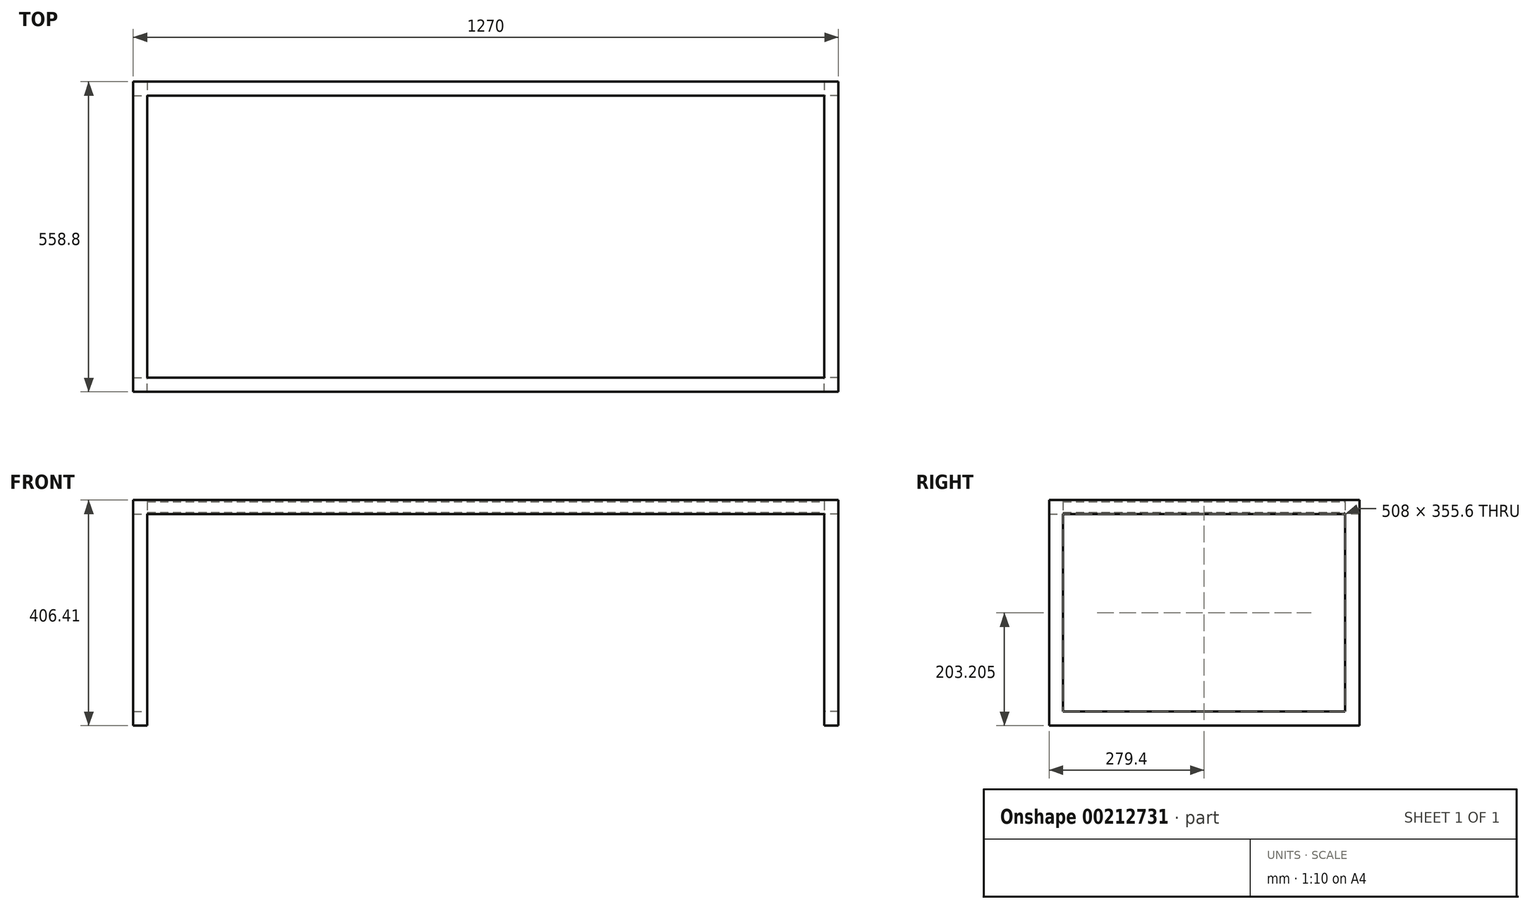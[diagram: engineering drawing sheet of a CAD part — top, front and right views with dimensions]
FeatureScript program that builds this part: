
annotation { "Feature Type Name" : "Feature", "Feature Type Description" : "" }
export const myFeature = defineFeature(function(context is Context, id is Id, definition is map)
    precondition{}
    {
        {
            var Q0;
            Q0=qCreatedBy(makeId("Top.planeOp"),FACE);
            var sketch = newSketch(context, id + "F0", { "sketchPlane" : qUnion([Q0])});
            skLineSegment(sketch, "E0.bottom", {"start": v(-609.6, -254) * mm, "end": v(609.6, -254) * mm});
            skLineSegment(sketch, "E0.top", {"start": v(-609.6, 254) * mm, "end": v(609.6, 254) * mm});
            skLineSegment(sketch, "E0.left", {"start": v(-609.6, -254) * mm, "end": v(-609.6, 254) * mm});
            skLineSegment(sketch, "E0.right", {"start": v(609.6, -254) * mm, "end": v(609.6, 254) * mm});
            skPoint(sketch, "E0.middle", {"position": v(0, 0) * mm});
            skSolve(sketch);
        }
        {
            var Q0;
            Q0=makeQuery(id+"F0.imprint","IMPRINT",FACE,{"disambiguationData":[TD([[makeQuery(id+"F0.imprint","IMPRINT",EDGE,{"derivedFrom":sQuery(id+"F0.wireOp",EDGE,"E0.bottom")}),1.0]])]});
            extrude(context, id + "F1", {"entities" : qUnion([Q0]), "depth" : 19.05 * mm});
        }
        {
            var Q0;
            Q0=makeQuery(id+"F1.opExtrude","CAP_FACE",FACE,{"disambiguationData":[OSD([sQuery(id+"F0.wireOp",EDGE,"E0.bottom"),sQuery(id+"F0.wireOp",EDGE,"E0.top"),sQuery(id+"F0.wireOp",EDGE,"E0.left"),sQuery(id+"F0.wireOp",EDGE,"E0.right")])],"isStart":true});
            cPlane(context, id + "F2", {"entities" : qUnion([Q0]), "cplaneType" : CPlaneType.OFFSET, "offset" : 3.17 * mm, "width" : 152.4 * mm, "height" : 152.4 * mm});
        }
        {
            var Q0;
            Q0=qCreatedBy(id+"F2.planeOp",FACE);
            var sketch = newSketch(context, id + "F3", { "sketchPlane" : qUnion([Q0])});
            skLineSegment(sketch, "E1.0.0", {"start": v(-609.6, -254) * mm, "end": v(609.6, -254) * mm});
            skLineSegment(sketch, "E1.0.1", {"start": v(609.6, -254) * mm, "end": v(609.6, 254) * mm});
            skLineSegment(sketch, "E1.0.2", {"start": v(609.6, 254) * mm, "end": v(-609.6, 254) * mm});
            skLineSegment(sketch, "E1.0.3", {"start": v(-609.6, 254) * mm, "end": v(-609.6, -254) * mm});
            skLineSegment(sketch, "E2.0", {"start": v(-635, -279.4) * mm, "end": v(635, -279.4) * mm});
            skLineSegment(sketch, "E2.1", {"start": v(-635, 279.4) * mm, "end": v(-635, -279.4) * mm});
            skLineSegment(sketch, "E2.2", {"start": v(635, 279.4) * mm, "end": v(-635, 279.4) * mm});
            skLineSegment(sketch, "E2.3", {"start": v(635, -279.4) * mm, "end": v(635, 279.4) * mm});
            skSolve(sketch);
        }
        {
            var Q0;
            Q0=makeQuery(id+"F3.imprint","IMPRINT",FACE,{"disambiguationData":[TD([[makeQuery(id+"F3.imprint","IMPRINT",EDGE,{"derivedFrom":sQuery(id+"F3.wireOp",EDGE,"E1.0.0")}),-1.0]])]});
            extrude(context, id + "F4", {"entities" : qUnion([Q0]), "oppositeDirection" : true, "depth" : 25.4 * mm});
        }
        {
            var Q0;
            Q0=makeQuery(id+"F4.opExtrude","CAP_FACE",FACE,{"disambiguationData":[OSD([sQuery(id+"F3.wireOp",EDGE,"E1.0.0"),sQuery(id+"F3.wireOp",EDGE,"E1.0.1"),sQuery(id+"F3.wireOp",EDGE,"E1.0.2"),sQuery(id+"F3.wireOp",EDGE,"E1.0.3"),sQuery(id+"F3.wireOp",EDGE,"E2.0"),sQuery(id+"F3.wireOp",EDGE,"E2.1"),sQuery(id+"F3.wireOp",EDGE,"E2.2"),sQuery(id+"F3.wireOp",EDGE,"E2.3")])],"isStart":true});
            var sketch = newSketch(context, id + "F5", { "sketchPlane" : qUnion([Q0])});
            skLineSegment(sketch, "E3.bottom", {"start": v(-635, 279.4) * mm, "end": v(-609.6, 279.4) * mm});
            skLineSegment(sketch, "E3.top", {"start": v(-635, 254) * mm, "end": v(-609.6, 254) * mm});
            skLineSegment(sketch, "E3.left", {"start": v(-635, 279.4) * mm, "end": v(-635, 254) * mm});
            skLineSegment(sketch, "E3.right", {"start": v(-609.6, 279.4) * mm, "end": v(-609.6, 254) * mm});
            skLineSegment(sketch, "E4.bottom", {"start": v(-635, -279.4) * mm, "end": v(-609.6, -279.4) * mm});
            skLineSegment(sketch, "E4.top", {"start": v(-635, -254) * mm, "end": v(-609.6, -254) * mm});
            skLineSegment(sketch, "E4.left", {"start": v(-635, -279.4) * mm, "end": v(-635, -254) * mm});
            skLineSegment(sketch, "E4.right", {"start": v(-609.6, -279.4) * mm, "end": v(-609.6, -254) * mm});
            skLineSegment(sketch, "E5.bottom", {"start": v(635, -279.4) * mm, "end": v(609.6, -279.4) * mm});
            skLineSegment(sketch, "E5.top", {"start": v(635, -254) * mm, "end": v(609.6, -254) * mm});
            skLineSegment(sketch, "E5.left", {"start": v(635, -279.4) * mm, "end": v(635, -254) * mm});
            skLineSegment(sketch, "E5.right", {"start": v(609.6, -279.4) * mm, "end": v(609.6, -254) * mm});
            skLineSegment(sketch, "E6.bottom", {"start": v(635, 279.4) * mm, "end": v(609.6, 279.4) * mm});
            skLineSegment(sketch, "E6.top", {"start": v(635, 254) * mm, "end": v(609.6, 254) * mm});
            skLineSegment(sketch, "E6.left", {"start": v(635, 279.4) * mm, "end": v(635, 254) * mm});
            skLineSegment(sketch, "E6.right", {"start": v(609.6, 279.4) * mm, "end": v(609.6, 254) * mm});
            skSolve(sketch);
        }
        {
            var Q0;
            Q0=makeQuery(id+"F5.imprint","IMPRINT",FACE,{"disambiguationData":[TD([[makeQuery(id+"F5.imprint","IMPRINT",EDGE,{"derivedFrom":sQuery(id+"F5.wireOp",EDGE,"E5.bottom")}),1.0]])]});
            var Q1;
            Q1=makeQuery(id+"F5.imprint","IMPRINT",FACE,{"disambiguationData":[TD([[makeQuery(id+"F5.imprint","IMPRINT",EDGE,{"derivedFrom":sQuery(id+"F5.wireOp",EDGE,"E6.bottom")}),1.0]])]});
            var Q2;
            Q2=makeQuery(id+"F5.imprint","IMPRINT",FACE,{"disambiguationData":[TD([[makeQuery(id+"F5.imprint","IMPRINT",EDGE,{"derivedFrom":sQuery(id+"F5.wireOp",EDGE,"E3.bottom")}),1.0]])]});
            var Q3;
            Q3=makeQuery(id+"F5.imprint","IMPRINT",FACE,{"disambiguationData":[TD([[makeQuery(id+"F5.imprint","IMPRINT",EDGE,{"derivedFrom":sQuery(id+"F5.wireOp",EDGE,"E4.bottom")}),1.0]])]});
            extrude(context, id + "F6", {"entities" : qUnion([Q0, Q1, Q2, Q3]), "operationType" : NewBodyOperationType.ADD, "depth" : 381 * mm});
        }
        {
            var Q0;
            Q0=makeQuery(id+"F6.opExtrude","SWEPT_FACE",FACE,{"disambiguationData":[OSD([sQuery(id+"F5.wireOp",EDGE,"E4.top")])]});
            var sketch = newSketch(context, id + "F7", { "sketchPlane" : qUnion([Q0])});
            skLineSegment(sketch, "E7.bottom", {"start": v(-635, -384.18) * mm, "end": v(-609.6, -384.18) * mm});
            skLineSegment(sketch, "E7.top", {"start": v(-635, -358.78) * mm, "end": v(-609.6, -358.78) * mm});
            skLineSegment(sketch, "E7.left", {"start": v(-635, -384.18) * mm, "end": v(-635, -358.78) * mm});
            skLineSegment(sketch, "E7.right", {"start": v(-609.6, -384.18) * mm, "end": v(-609.6, -358.78) * mm});
            skPoint(sketch, "E8.0", {"position": v(635, -384.18) * mm});
            skLineSegment(sketch, "E9.bottom", {"start": v(635, -384.18) * mm, "end": v(609.6, -384.18) * mm});
            skLineSegment(sketch, "E9.top", {"start": v(635, -358.78) * mm, "end": v(609.6, -358.78) * mm});
            skLineSegment(sketch, "E9.left", {"start": v(635, -384.18) * mm, "end": v(635, -358.78) * mm});
            skLineSegment(sketch, "E9.right", {"start": v(609.6, -384.18) * mm, "end": v(609.6, -358.78) * mm});
            skSolve(sketch);
        }
        {
            var Q0;
            Q0=makeQuery(id+"F7.imprint","IMPRINT",FACE,{"disambiguationData":[TD([[makeQuery(id+"F7.imprint","IMPRINT",EDGE,{"derivedFrom":sQuery(id+"F7.wireOp",EDGE,"E9.bottom")}),-1.0]])]});
            var Q1;
            Q1=makeQuery(id+"F7.imprint","IMPRINT",FACE,{"disambiguationData":[TD([[makeQuery(id+"F7.imprint","IMPRINT",EDGE,{"derivedFrom":sQuery(id+"F7.wireOp",EDGE,"E7.bottom")}),1.0]])]});
            extrude(context, id + "F8", {"entities" : qUnion([Q0, Q1]), "operationType" : NewBodyOperationType.ADD, "depth" : 508 * mm});
        }
    });
